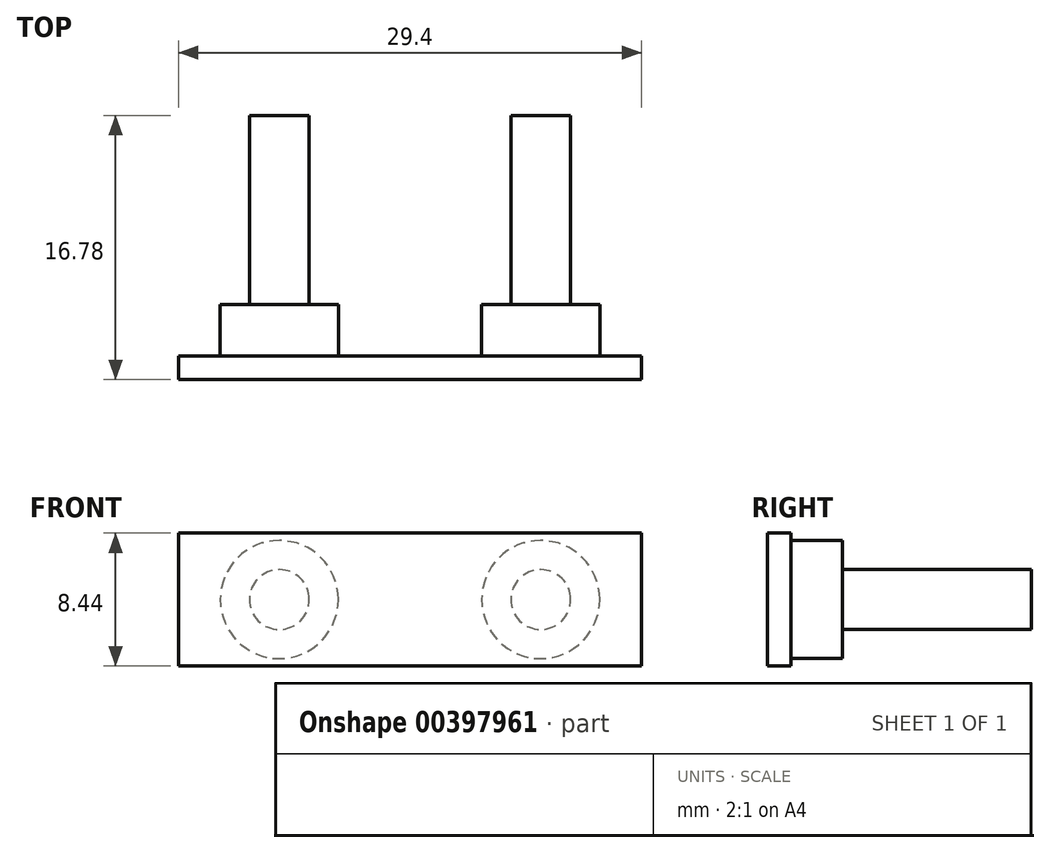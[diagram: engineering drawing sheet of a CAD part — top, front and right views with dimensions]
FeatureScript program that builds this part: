
annotation { "Feature Type Name" : "Feature", "Feature Type Description" : "" }
export const myFeature = defineFeature(function(context is Context, id is Id, definition is map)
    precondition{}
    {
        {
            var Q0;
            Q0=qCreatedBy(makeId("Front.planeOp"),FACE);
            var sketch = newSketch(context, id + "F0", { "sketchPlane" : qUnion([Q0])});
            skLineSegment(sketch, "E0", {"start": v(-10.9, 0) * mm, "end": v(10.38, 0) * mm, "construction": true});
            skCircle(sketch, "E1", {"center": v(-8.3, 0) * mm, "radius": 1.9 * mm});
            skCircle(sketch, "E2", {"center": v(8.3, 0) * mm, "radius": 1.9 * mm});
            skLineSegment(sketch, "E3.bottom", {"start": v(-14.7, 4.22) * mm, "end": v(14.7, 4.22) * mm});
            skLineSegment(sketch, "E3.top", {"start": v(-14.7, -4.22) * mm, "end": v(14.7, -4.22) * mm});
            skLineSegment(sketch, "E3.left", {"start": v(-14.7, 4.22) * mm, "end": v(-14.7, -4.22) * mm});
            skLineSegment(sketch, "E3.right", {"start": v(14.7, 4.22) * mm, "end": v(14.7, -4.22) * mm});
            skPoint(sketch, "E3.middle", {"position": v(0, 0) * mm});
            skLineSegment(sketch, "E4", {"start": v(-8.3, 4.07) * mm, "end": v(-8.3, -4.07) * mm, "construction": true});
            skLineSegment(sketch, "E5", {"start": v(8.3, 4.07) * mm, "end": v(8.3, -4.07) * mm, "construction": true});
            skCircle(sketch, "E6", {"center": v(-8.3, 0) * mm, "radius": 3.75 * mm});
            skCircle(sketch, "E7", {"center": v(8.3, 0) * mm, "radius": 3.75 * mm});
            skSolve(sketch);
        }
        {
            var Q0;
            Q0=makeQuery(id+"F0.imprint","IMPRINT",FACE,{"disambiguationData":[TD([[makeQuery(id+"F0.imprint","IMPRINT",EDGE,{"derivedFrom":sQuery(id+"F0.wireOp",EDGE,"E3.bottom")}),-1.0]])]});
            var Q1;
            Q1=makeQuery(id+"F0.imprint","IMPRINT",FACE,{"disambiguationData":[TD([[makeQuery(id+"F0.imprint","IMPRINT",EDGE,{"derivedFrom":sQuery(id+"F0.wireOp",EDGE,"E1")}),-1.0]])]});
            var Q2;
            Q2=makeQuery(id+"F0.imprint","IMPRINT",FACE,{"disambiguationData":[TD([[makeQuery(id+"F0.imprint","IMPRINT",EDGE,{"derivedFrom":sQuery(id+"F0.wireOp",EDGE,"E1")}),1.0]])]});
            var Q3;
            Q3=makeQuery(id+"F0.imprint","IMPRINT",FACE,{"disambiguationData":[TD([[makeQuery(id+"F0.imprint","IMPRINT",EDGE,{"derivedFrom":sQuery(id+"F0.wireOp",EDGE,"E2")}),-1.0]])]});
            var Q4;
            Q4=makeQuery(id+"F0.imprint","IMPRINT",FACE,{"disambiguationData":[TD([[makeQuery(id+"F0.imprint","IMPRINT",EDGE,{"derivedFrom":sQuery(id+"F0.wireOp",EDGE,"E2")}),1.0]])]});
            extrude(context, id + "F1", {"entities" : qUnion([Q0, Q1, Q2, Q3, Q4]), "depth" : 11.78 * mm});
        }
        {
            var Q0;
            Q0=makeQuery(id+"F0.imprint","IMPRINT",FACE,{"disambiguationData":[TD([[makeQuery(id+"F0.imprint","IMPRINT",EDGE,{"derivedFrom":sQuery(id+"F0.wireOp",EDGE,"E3.bottom")}),-1.0]])]});
            extrude(context, id + "F2", {"entities" : qUnion([Q0]), "operationType" : NewBodyOperationType.REMOVE, "depth" : 10.28 * mm});
        }
        {
            var Q0;
            Q0=makeQuery(id+"F0.imprint","IMPRINT",FACE,{"disambiguationData":[TD([[makeQuery(id+"F0.imprint","IMPRINT",EDGE,{"derivedFrom":sQuery(id+"F0.wireOp",EDGE,"E1")}),-1.0]])]});
            var Q1;
            Q1=makeQuery(id+"F0.imprint","IMPRINT",FACE,{"disambiguationData":[TD([[makeQuery(id+"F0.imprint","IMPRINT",EDGE,{"derivedFrom":sQuery(id+"F0.wireOp",EDGE,"E2")}),-1.0]])]});
            extrude(context, id + "F3", {"entities" : qUnion([Q0, Q1]), "operationType" : NewBodyOperationType.REMOVE, "depth" : 7 * mm});
        }
        {
            var Q0;
            Q0=makeQuery(id+"F0.imprint","IMPRINT",FACE,{"disambiguationData":[TD([[makeQuery(id+"F0.imprint","IMPRINT",EDGE,{"derivedFrom":sQuery(id+"F0.wireOp",EDGE,"E1")}),1.0]])]});
            var Q1;
            Q1=makeQuery(id+"F0.imprint","IMPRINT",FACE,{"disambiguationData":[TD([[makeQuery(id+"F0.imprint","IMPRINT",EDGE,{"derivedFrom":sQuery(id+"F0.wireOp",EDGE,"E2")}),1.0]])]});
            extrude(context, id + "F4", {"entities" : qUnion([Q0, Q1]), "operationType" : NewBodyOperationType.ADD, "oppositeDirection" : true, "depth" : 5 * mm});
        }
    });
